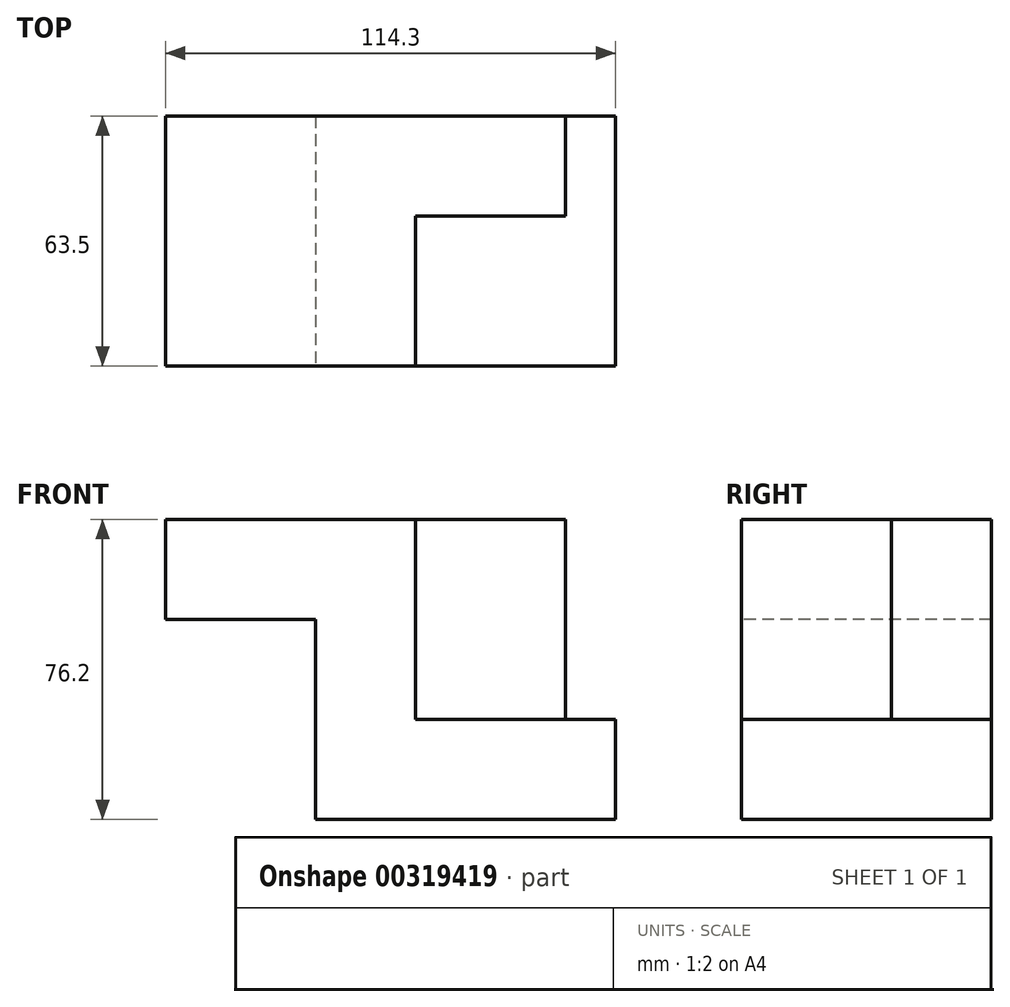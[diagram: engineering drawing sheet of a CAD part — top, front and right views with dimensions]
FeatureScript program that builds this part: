
annotation { "Feature Type Name" : "Feature", "Feature Type Description" : "" }
export const myFeature = defineFeature(function(context is Context, id is Id, definition is map)
    precondition{}
    {
        {
            var Q0;
            Q0=qCreatedBy(makeId("Top.planeOp"),FACE);
            var sketch = newSketch(context, id + "F0", { "sketchPlane" : qUnion([Q0])});
            skLineSegment(sketch, "E0.bottom", {"start": v(-57.05, 33.2) * mm, "end": v(19.15, 33.2) * mm});
            skLineSegment(sketch, "E0.top", {"start": v(-57.05, -30.3) * mm, "end": v(19.15, -30.3) * mm});
            skLineSegment(sketch, "E0.left", {"start": v(-57.05, 33.2) * mm, "end": v(-57.05, -30.3) * mm});
            skLineSegment(sketch, "E0.right", {"start": v(19.15, 33.2) * mm, "end": v(19.15, -30.3) * mm});
            skSolve(sketch);
        }
        {
            var Q0;
            Q0=makeQuery(id+"F0.imprint","IMPRINT",FACE,{"disambiguationData":[TD([[makeQuery(id+"F0.imprint","IMPRINT",EDGE,{"derivedFrom":sQuery(id+"F0.wireOp",EDGE,"E0.bottom")}),-1.0]])]});
            extrude(context, id + "F1", {"entities" : qUnion([Q0]), "depth" : 25.4 * mm});
        }
        {
            var Q0;
            Q0=makeQuery(id+"F1.opExtrude","CAP_FACE",FACE,{"disambiguationData":[OSD([sQuery(id+"F0.wireOp",EDGE,"E0.bottom"),sQuery(id+"F0.wireOp",EDGE,"E0.top"),sQuery(id+"F0.wireOp",EDGE,"E0.left"),sQuery(id+"F0.wireOp",EDGE,"E0.right")])],"isStart":false});
            var sketch = newSketch(context, id + "F2", { "sketchPlane" : qUnion([Q0])});
            skLineSegment(sketch, "E1", {"start": v(-57.05, -30.3) * mm, "end": v(-57.05, 33.2) * mm});
            skLineSegment(sketch, "E2", {"start": v(-57.05, -30.3) * mm, "end": v(-31.65, -30.3) * mm});
            skLineSegment(sketch, "E3", {"start": v(-31.65, -30.3) * mm, "end": v(-31.65, 7.8) * mm});
            skLineSegment(sketch, "E4", {"start": v(-31.65, 7.8) * mm, "end": v(6.45, 7.8) * mm});
            skLineSegment(sketch, "E5", {"start": v(6.45, 7.8) * mm, "end": v(6.45, 33.2) * mm});
            skLineSegment(sketch, "E6", {"start": v(6.45, 33.2) * mm, "end": v(-57.05, 33.2) * mm});
            skLineSegment(sketch, "E7", {"start": v(-57.05, 33.2) * mm, "end": v(-57.05, -30.3) * mm});
            skSolve(sketch);
        }
        {
            var Q0;
            Q0=makeQuery(id+"F2.imprint","IMPRINT",FACE,{"disambiguationData":[TD([[makeQuery(id+"F2.imprint","IMPRINT",EDGE,{"derivedFrom":sQuery(id+"F2.wireOp",EDGE,"E2")}),1.0]])]});
            extrude(context, id + "F3", {"entities" : qUnion([Q0]), "operationType" : NewBodyOperationType.ADD, "depth" : 50.8 * mm});
        }
        {
            var Q0;
            Q0=makeQuery(id+"F3.boolean.opBoolean","MERGE",FACE,{"derivedFrom":[makeQuery(id+"F1.opExtrude","SWEPT_FACE",FACE,{"disambiguationData":[OSD([sQuery(id+"F0.wireOp",EDGE,"E0.top")])]}),makeQuery(id+"F3.opExtrude","SWEPT_FACE",FACE,{"disambiguationData":[OSD([sQuery(id+"F2.wireOp",EDGE,"E2")])]})]});
            var sketch = newSketch(context, id + "F4", { "sketchPlane" : qUnion([Q0])});
            skLineSegment(sketch, "E8", {"start": v(-57.05, 76.2) * mm, "end": v(-57.05, 50.8) * mm});
            skLineSegment(sketch, "E9", {"start": v(-57.05, 50.8) * mm, "end": v(-95.15, 50.8) * mm});
            skLineSegment(sketch, "E10", {"start": v(-95.15, 50.8) * mm, "end": v(-95.15, 76.2) * mm});
            skLineSegment(sketch, "E11", {"start": v(-95.15, 76.2) * mm, "end": v(-57.05, 76.2) * mm});
            skSolve(sketch);
        }
        {
            var Q0;
            Q0=makeQuery(id+"F4.imprint","IMPRINT",FACE,{"disambiguationData":[TD([[makeQuery(id+"F4.imprint","IMPRINT",EDGE,{"derivedFrom":sQuery(id+"F4.wireOp",EDGE,"E8")}),-1.0]])]});
            extrude(context, id + "F5", {"entities" : qUnion([Q0]), "operationType" : NewBodyOperationType.ADD, "oppositeDirection" : true, "depth" : 63.5 * mm});
        }
    });
